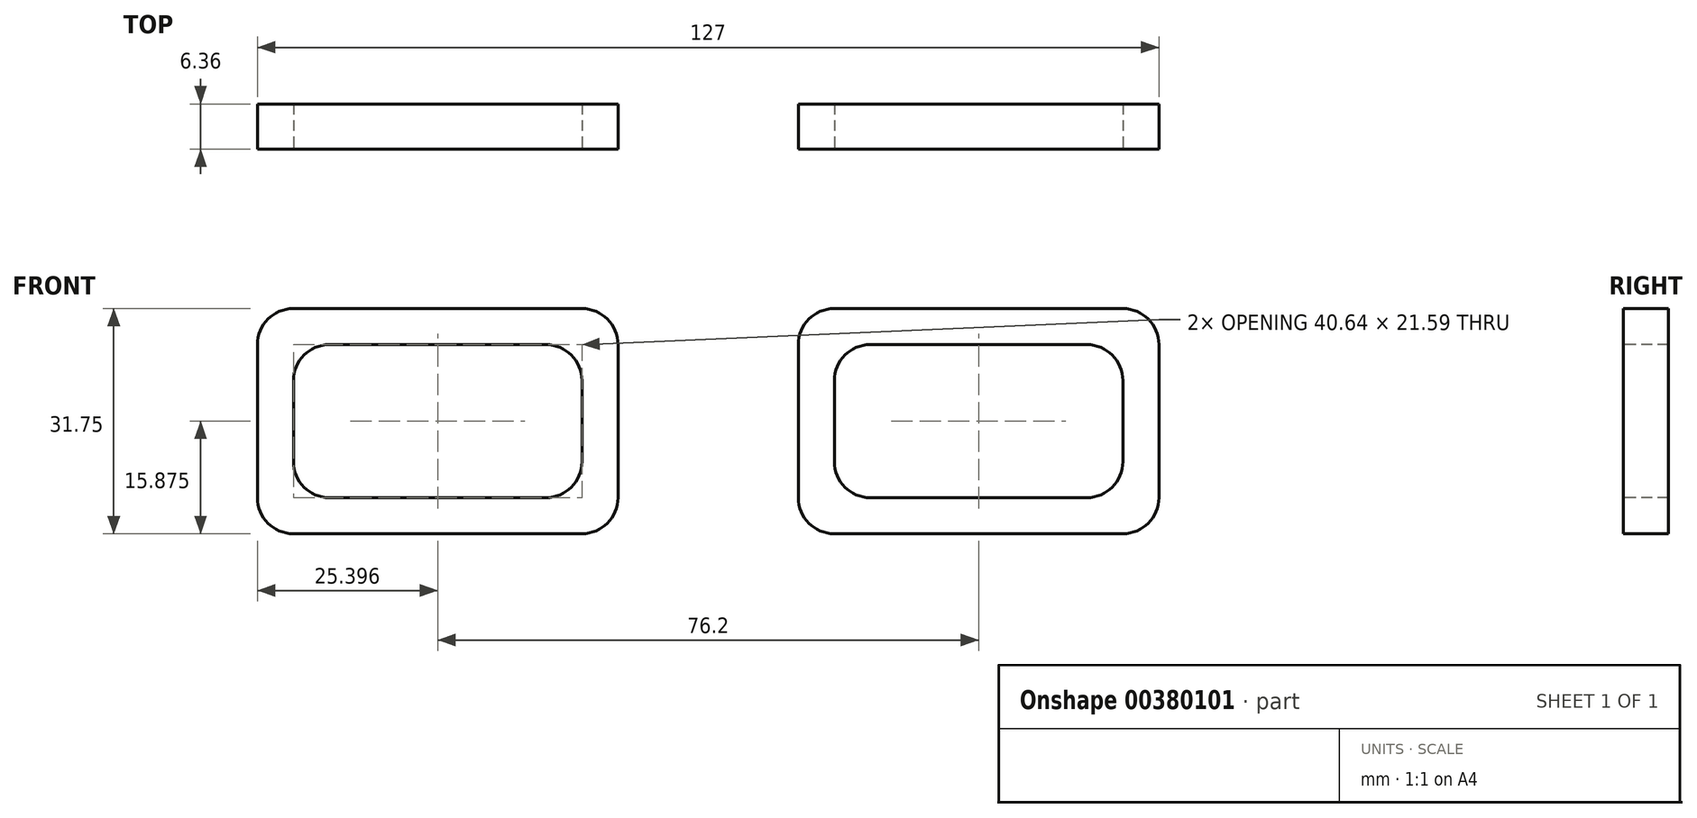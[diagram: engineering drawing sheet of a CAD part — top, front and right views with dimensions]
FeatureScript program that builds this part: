
annotation { "Feature Type Name" : "Feature", "Feature Type Description" : "" }
export const myFeature = defineFeature(function(context is Context, id is Id, definition is map)
    precondition{}
    {
        {
            var Q0;
            Q0=qCreatedBy(makeId("Front.planeOp"),FACE);
            var sketch = newSketch(context, id + "F0", { "sketchPlane" : qUnion([Q0])});
            skLineSegment(sketch, "E0.bottom", {"start": v(-73.86, 37.3) * mm, "end": v(-23.06, 37.3) * mm});
            skLineSegment(sketch, "E0.top", {"start": v(-73.86, 5.55) * mm, "end": v(-23.06, 5.55) * mm});
            skLineSegment(sketch, "E0.left", {"start": v(-73.86, 37.3) * mm, "end": v(-73.86, 5.55) * mm});
            skLineSegment(sketch, "E0.right", {"start": v(-23.06, 37.3) * mm, "end": v(-23.06, 5.55) * mm});
            skLineSegment(sketch, "E1.bottom", {"start": v(2.34, 37.3) * mm, "end": v(53.14, 37.3) * mm});
            skLineSegment(sketch, "E1.top", {"start": v(2.34, 5.55) * mm, "end": v(53.14, 5.55) * mm});
            skLineSegment(sketch, "E1.left", {"start": v(2.34, 37.3) * mm, "end": v(2.34, 5.55) * mm});
            skLineSegment(sketch, "E1.right", {"start": v(53.14, 37.3) * mm, "end": v(53.14, 5.55) * mm});
            skSolve(sketch);
        }
        {
            var Q0;
            Q0 = qSketchRegion(id + "F0", true);
            extrude(context, id + "F1", {"entities" : qUnion([Q0]), "endBound" : BoundingType.SYMMETRIC, "depth" : 6.35 * mm});
        }
        {
            var Q0;
            Q0=makeQuery(id+"F1.opExtrude","SWEPT_EDGE",EDGE,{"disambiguationData":[OSD([sQuery(id+"F0.wireOp",EDGE,"E0.bottom"),sQuery(id+"F0.wireOp",EDGE,"E0.left")])]});
            var Q1;
            Q1=makeQuery(id+"F1.opExtrude","SWEPT_EDGE",EDGE,{"disambiguationData":[OSD([sQuery(id+"F0.wireOp",EDGE,"E0.top"),sQuery(id+"F0.wireOp",EDGE,"E0.left")])]});
            var Q2;
            Q2=makeQuery(id+"F1.opExtrude","SWEPT_EDGE",EDGE,{"disambiguationData":[OSD([sQuery(id+"F0.wireOp",EDGE,"E0.top"),sQuery(id+"F0.wireOp",EDGE,"E0.right")])]});
            var Q3;
            Q3=makeQuery(id+"F1.opExtrude","SWEPT_EDGE",EDGE,{"disambiguationData":[OSD([sQuery(id+"F0.wireOp",EDGE,"E0.bottom"),sQuery(id+"F0.wireOp",EDGE,"E0.right")])]});
            var Q4;
            Q4=makeQuery(id+"F1.opExtrude","SWEPT_EDGE",EDGE,{"disambiguationData":[OSD([sQuery(id+"F0.wireOp",EDGE,"E1.bottom"),sQuery(id+"F0.wireOp",EDGE,"E1.left")])]});
            var Q5;
            Q5=makeQuery(id+"F1.opExtrude","SWEPT_EDGE",EDGE,{"disambiguationData":[OSD([sQuery(id+"F0.wireOp",EDGE,"E1.bottom"),sQuery(id+"F0.wireOp",EDGE,"E1.right")])]});
            var Q6;
            Q6=makeQuery(id+"F1.opExtrude","SWEPT_EDGE",EDGE,{"disambiguationData":[OSD([sQuery(id+"F0.wireOp",EDGE,"E1.top"),sQuery(id+"F0.wireOp",EDGE,"E1.right")])]});
            var Q7;
            Q7=makeQuery(id+"F1.opExtrude","SWEPT_EDGE",EDGE,{"disambiguationData":[OSD([sQuery(id+"F0.wireOp",EDGE,"E1.top"),sQuery(id+"F0.wireOp",EDGE,"E1.left")])]});
            fillet(context, id + "F2", {"entities" : qUnion([Q0, Q1, Q2, Q3, Q4, Q5, Q6, Q7]), "radius" : 5.08 * mm, "tangentPropagation" : true, "allowEdgeOverflow" : false});
        }
        {
            var Q0;
            Q0=makeQuery(id+"F1.opExtrude","CAP_FACE",FACE,{"disambiguationData":[OSD([sQuery(id+"F0.wireOp",EDGE,"E0.bottom"),sQuery(id+"F0.wireOp",EDGE,"E0.top"),sQuery(id+"F0.wireOp",EDGE,"E0.left"),sQuery(id+"F0.wireOp",EDGE,"E0.right")])],"isStart":false});
            var sketch = newSketch(context, id + "F3", { "sketchPlane" : qUnion([Q0])});
            skLineSegment(sketch, "E2.bottom", {"start": v(-68.78, 32.22) * mm, "end": v(-28.14, 32.22) * mm});
            skLineSegment(sketch, "E2.top", {"start": v(-68.78, 10.63) * mm, "end": v(-28.14, 10.63) * mm});
            skLineSegment(sketch, "E2.left", {"start": v(-68.78, 32.22) * mm, "end": v(-68.78, 10.63) * mm});
            skLineSegment(sketch, "E2.right", {"start": v(-28.14, 32.22) * mm, "end": v(-28.14, 10.63) * mm});
            skSolve(sketch);
        }
        {
            var Q0;
            Q0 = qSketchRegion(id + "F3", true);
            extrude(context, id + "F4", {"entities" : qUnion([Q0]), "operationType" : NewBodyOperationType.REMOVE, "oppositeDirection" : true, "depth" : 25.4 * mm});
        }
        {
            var Q0;
            Q0=makeQuery(id+"F4.boolean.opBoolean","COPY",EDGE,{"derivedFrom":makeQuery(id+"F4.opExtrude","SWEPT_EDGE",EDGE,{"disambiguationData":[OSD([sQuery(id+"F3.wireOp",EDGE,"E2.bottom"),sQuery(id+"F3.wireOp",EDGE,"E2.right")])]})});
            var Q1;
            Q1=makeQuery(id+"F4.boolean.opBoolean","COPY",EDGE,{"derivedFrom":makeQuery(id+"F4.opExtrude","SWEPT_EDGE",EDGE,{"disambiguationData":[OSD([sQuery(id+"F3.wireOp",EDGE,"E2.top"),sQuery(id+"F3.wireOp",EDGE,"E2.left")])]})});
            var Q2;
            Q2=makeQuery(id+"F4.boolean.opBoolean","COPY",EDGE,{"derivedFrom":makeQuery(id+"F4.opExtrude","SWEPT_EDGE",EDGE,{"disambiguationData":[OSD([sQuery(id+"F3.wireOp",EDGE,"E2.bottom"),sQuery(id+"F3.wireOp",EDGE,"E2.left")])]})});
            var Q3;
            Q3=makeQuery(id+"F4.boolean.opBoolean","COPY",EDGE,{"derivedFrom":makeQuery(id+"F4.opExtrude","SWEPT_EDGE",EDGE,{"disambiguationData":[OSD([sQuery(id+"F3.wireOp",EDGE,"E2.top"),sQuery(id+"F3.wireOp",EDGE,"E2.right")])]})});
            fillet(context, id + "F5", {"entities" : qUnion([Q0, Q1, Q2, Q3]), "radius" : 5.08 * mm, "tangentPropagation" : true, "allowEdgeOverflow" : false});
        }
        {
            var Q0;
            Q0=makeQuery(id+"F1.opExtrude","CAP_FACE",FACE,{"disambiguationData":[OSD([sQuery(id+"F0.wireOp",EDGE,"E1.bottom"),sQuery(id+"F0.wireOp",EDGE,"E1.top"),sQuery(id+"F0.wireOp",EDGE,"E1.left"),sQuery(id+"F0.wireOp",EDGE,"E1.right")])],"isStart":false});
            var sketch = newSketch(context, id + "F6", { "sketchPlane" : qUnion([Q0])});
            skLineSegment(sketch, "E3.bottom", {"start": v(7.42, 32.22) * mm, "end": v(48.06, 32.22) * mm});
            skLineSegment(sketch, "E3.top", {"start": v(7.42, 10.63) * mm, "end": v(48.06, 10.63) * mm});
            skLineSegment(sketch, "E3.left", {"start": v(7.42, 32.22) * mm, "end": v(7.42, 10.63) * mm});
            skLineSegment(sketch, "E3.right", {"start": v(48.06, 32.22) * mm, "end": v(48.06, 10.63) * mm});
            skSolve(sketch);
        }
        {
            var Q0;
            Q0 = qSketchRegion(id + "F6", true);
            extrude(context, id + "F7", {"entities" : qUnion([Q0]), "operationType" : NewBodyOperationType.REMOVE, "oppositeDirection" : true, "depth" : 25.4 * mm});
        }
        {
            var Q0;
            Q0=makeQuery(id+"F7.boolean.opBoolean","COPY",EDGE,{"derivedFrom":makeQuery(id+"F7.opExtrude","SWEPT_EDGE",EDGE,{"disambiguationData":[OSD([sQuery(id+"F6.wireOp",EDGE,"E3.top"),sQuery(id+"F6.wireOp",EDGE,"E3.right")])]})});
            var Q1;
            Q1=makeQuery(id+"F7.boolean.opBoolean","COPY",EDGE,{"derivedFrom":makeQuery(id+"F7.opExtrude","SWEPT_EDGE",EDGE,{"disambiguationData":[OSD([sQuery(id+"F6.wireOp",EDGE,"E3.top"),sQuery(id+"F6.wireOp",EDGE,"E3.left")])]})});
            var Q2;
            Q2=makeQuery(id+"F7.boolean.opBoolean","COPY",EDGE,{"derivedFrom":makeQuery(id+"F7.opExtrude","SWEPT_EDGE",EDGE,{"disambiguationData":[OSD([sQuery(id+"F6.wireOp",EDGE,"E3.bottom"),sQuery(id+"F6.wireOp",EDGE,"E3.left")])]})});
            var Q3;
            Q3=makeQuery(id+"F7.boolean.opBoolean","COPY",EDGE,{"derivedFrom":makeQuery(id+"F7.opExtrude","SWEPT_EDGE",EDGE,{"disambiguationData":[OSD([sQuery(id+"F6.wireOp",EDGE,"E3.bottom"),sQuery(id+"F6.wireOp",EDGE,"E3.right")])]})});
            fillet(context, id + "F8", {"entities" : qUnion([Q0, Q1, Q2, Q3]), "radius" : 5.08 * mm, "tangentPropagation" : true, "allowEdgeOverflow" : false});
        }
    });
